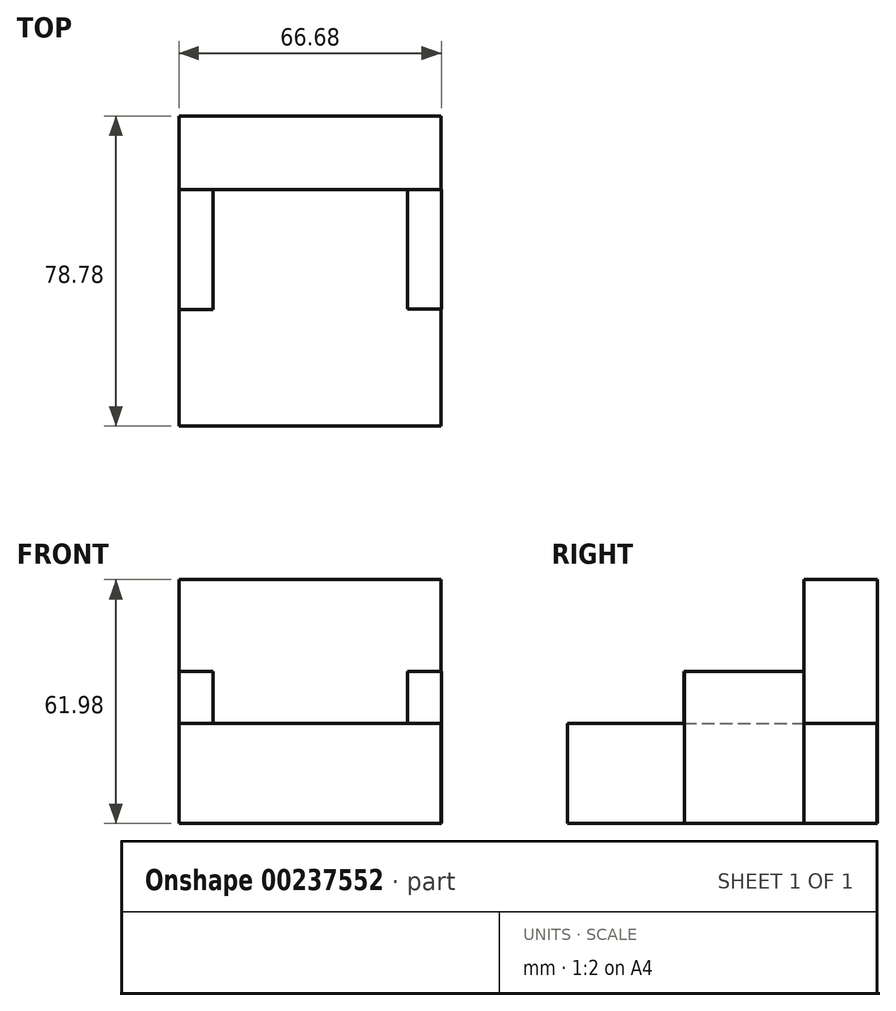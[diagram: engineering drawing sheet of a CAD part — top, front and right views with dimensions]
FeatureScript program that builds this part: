
annotation { "Feature Type Name" : "Feature", "Feature Type Description" : "" }
export const myFeature = defineFeature(function(context is Context, id is Id, definition is map)
    precondition{}
    {
        {
            var Q0;
            Q0=qCreatedBy(makeId("Top.planeOp"),FACE);
            var sketch = newSketch(context, id + "F0", { "sketchPlane" : qUnion([Q0])});
            skLineSegment(sketch, "E0.bottom", {"start": v(33.29, -39.35) * mm, "end": v(-33.29, -39.35) * mm});
            skLineSegment(sketch, "E0.top", {"start": v(33.29, 39.35) * mm, "end": v(-33.29, 39.35) * mm});
            skLineSegment(sketch, "E0.left", {"start": v(33.29, -39.35) * mm, "end": v(33.29, 39.35) * mm});
            skLineSegment(sketch, "E0.right", {"start": v(-33.29, -39.35) * mm, "end": v(-33.29, 39.35) * mm});
            skPoint(sketch, "E0.middle", {"position": v(0, 0) * mm});
            skSolve(sketch);
        }
        {
            var Q0;
            Q0 = qSketchRegion(id + "F0", true);
            extrude(context, id + "F1", {"entities" : qUnion([Q0]), "depth" : 25.4 * mm});
        }
        {
            var Q0;
            Q0=qCreatedBy(makeId("Top.planeOp"),FACE);
            var sketch = newSketch(context, id + "F2", { "sketchPlane" : qUnion([Q0])});
            skLineSegment(sketch, "E1.bottom", {"start": v(-33.32, 39.43) * mm, "end": v(33.2, 39.43) * mm});
            skLineSegment(sketch, "E1.top", {"start": v(-33.32, 20.78) * mm, "end": v(33.2, 20.78) * mm});
            skLineSegment(sketch, "E1.left", {"start": v(-33.32, 39.43) * mm, "end": v(-33.32, 20.78) * mm});
            skLineSegment(sketch, "E1.right", {"start": v(33.2, 39.43) * mm, "end": v(33.2, 20.78) * mm});
            skSolve(sketch);
        }
        {
            var Q0;
            Q0 = qSketchRegion(id + "F2", true);
            extrude(context, id + "F3", {"entities" : qUnion([Q0]), "operationType" : NewBodyOperationType.ADD, "depth" : 61.98 * mm});
        }
        {
            var Q0;
            Q0=qCreatedBy(makeId("Top.planeOp"),FACE);
            var sketch = newSketch(context, id + "F4", { "sketchPlane" : qUnion([Q0])});
            skLineSegment(sketch, "E2.bottom", {"start": v(-33.36, 20.8) * mm, "end": v(-24.67, 20.8) * mm});
            skLineSegment(sketch, "E2.top", {"start": v(-33.36, -9.74) * mm, "end": v(-24.67, -9.74) * mm});
            skLineSegment(sketch, "E2.left", {"start": v(-33.36, 20.8) * mm, "end": v(-33.36, -9.74) * mm});
            skLineSegment(sketch, "E2.right", {"start": v(-24.67, 20.8) * mm, "end": v(-24.67, -9.74) * mm});
            skSolve(sketch);
        }
        {
            var Q0;
            Q0 = qSketchRegion(id + "F4", true);
            extrude(context, id + "F5", {"entities" : qUnion([Q0]), "operationType" : NewBodyOperationType.ADD, "depth" : 38.6 * mm});
        }
        {
            var Q0;
            Q0=qCreatedBy(makeId("Top.planeOp"),FACE);
            var sketch = newSketch(context, id + "F6", { "sketchPlane" : qUnion([Q0])});
            skLineSegment(sketch, "E3.bottom", {"start": v(33.32, 20.73) * mm, "end": v(24.67, 20.73) * mm});
            skLineSegment(sketch, "E3.top", {"start": v(33.32, -9.55) * mm, "end": v(24.67, -9.55) * mm});
            skLineSegment(sketch, "E3.left", {"start": v(33.32, 20.73) * mm, "end": v(33.32, -9.55) * mm});
            skLineSegment(sketch, "E3.right", {"start": v(24.67, 20.73) * mm, "end": v(24.67, -9.55) * mm});
            skSolve(sketch);
        }
        {
            var Q0;
            Q0 = qSketchRegion(id + "F6", true);
            extrude(context, id + "F7", {"entities" : qUnion([Q0]), "operationType" : NewBodyOperationType.ADD, "depth" : 38.6 * mm});
        }
    });
